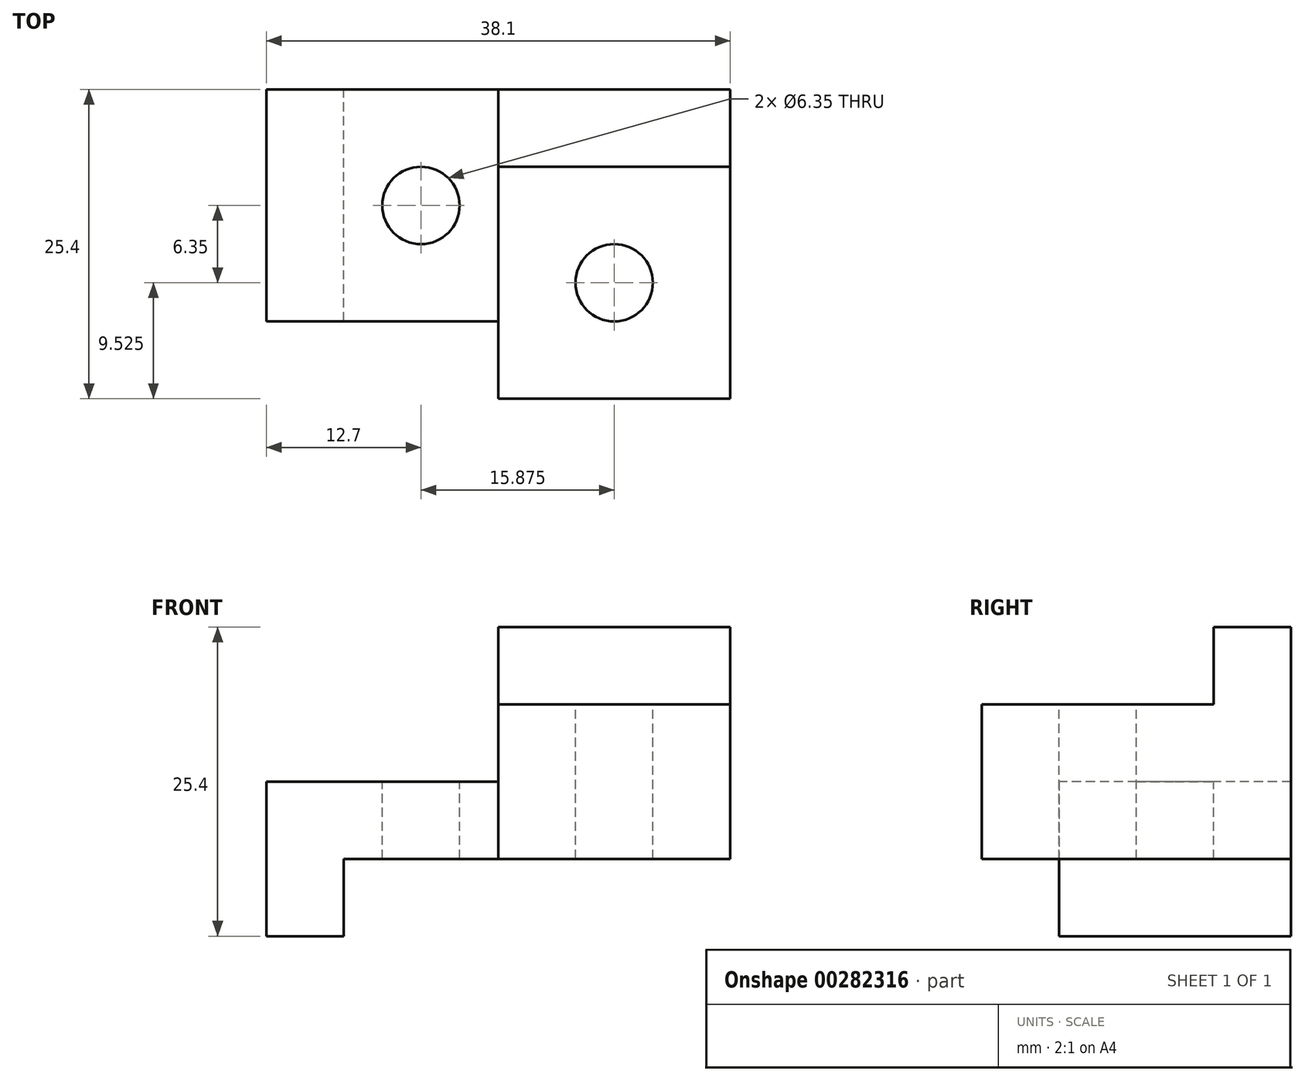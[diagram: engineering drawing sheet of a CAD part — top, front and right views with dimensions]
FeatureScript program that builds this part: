
annotation { "Feature Type Name" : "Feature", "Feature Type Description" : "" }
export const myFeature = defineFeature(function(context is Context, id is Id, definition is map)
    precondition{}
    {
        {
            var Q0;
            Q0=qCreatedBy(makeId("Top.planeOp"),FACE);
            var sketch = newSketch(context, id + "F0", { "sketchPlane" : qUnion([Q0])});
            skLineSegment(sketch, "E0", {"start": v(0, 0) * mm, "end": v(0, 6.35) * mm});
            skLineSegment(sketch, "E1", {"start": v(0, 6.35) * mm, "end": v(-19.05, 6.35) * mm});
            skLineSegment(sketch, "E2", {"start": v(-19.05, 6.35) * mm, "end": v(-19.05, 25.4) * mm});
            skLineSegment(sketch, "E3", {"start": v(-19.05, 25.4) * mm, "end": v(0, 25.4) * mm});
            skLineSegment(sketch, "E4", {"start": v(0, 25.4) * mm, "end": v(19.05, 25.4) * mm});
            skLineSegment(sketch, "E5", {"start": v(19.05, 0) * mm, "end": v(0, 0) * mm});
            skLineSegment(sketch, "E6", {"start": v(19.05, 25.4) * mm, "end": v(19.05, 0) * mm});
            skSolve(sketch);
        }
        {
            var Q0;
            Q0 = qSketchRegion(id + "F0", true);
            extrude(context, id + "F1", {"entities" : qUnion([Q0]), "depth" : 6.35 * mm});
        }
        {
            var Q0;
            Q0=makeQuery(id+"F1.opExtrude","CAP_FACE",FACE,{"disambiguationData":[OSD([sQuery(id+"F0.wireOp",EDGE,"E0"),sQuery(id+"F0.wireOp",EDGE,"E1"),sQuery(id+"F0.wireOp",EDGE,"E2"),sQuery(id+"F0.wireOp",EDGE,"E3"),sQuery(id+"F0.wireOp",EDGE,"E4"),sQuery(id+"F0.wireOp",EDGE,"E5"),sQuery(id+"F0.wireOp",EDGE,"E6")])],"isStart":true});
            var sketch = newSketch(context, id + "F2", { "sketchPlane" : qUnion([Q0])});
            skLineSegment(sketch, "E7", {"start": v(-19.05, -6.35) * mm, "end": v(-12.7, -6.35) * mm});
            skLineSegment(sketch, "E8", {"start": v(-12.7, -6.35) * mm, "end": v(-12.7, -25.4) * mm});
            skLineSegment(sketch, "E9", {"start": v(-12.7, -25.4) * mm, "end": v(-19.05, -25.4) * mm});
            skLineSegment(sketch, "E10", {"start": v(-19.05, -25.4) * mm, "end": v(-19.05, -6.35) * mm});
            skSolve(sketch);
        }
        {
            var Q0;
            Q0 = qSketchRegion(id + "F2", true);
            extrude(context, id + "F3", {"entities" : qUnion([Q0]), "operationType" : NewBodyOperationType.ADD, "depth" : 6.35 * mm});
        }
        {
            var Q0;
            Q0=makeQuery(id+"F1.opExtrude","CAP_FACE",FACE,{"disambiguationData":[OSD([sQuery(id+"F0.wireOp",EDGE,"E0"),sQuery(id+"F0.wireOp",EDGE,"E1"),sQuery(id+"F0.wireOp",EDGE,"E2"),sQuery(id+"F0.wireOp",EDGE,"E3"),sQuery(id+"F0.wireOp",EDGE,"E4"),sQuery(id+"F0.wireOp",EDGE,"E5"),sQuery(id+"F0.wireOp",EDGE,"E6")])],"isStart":false});
            var sketch = newSketch(context, id + "F4", { "sketchPlane" : qUnion([Q0])});
            skLineSegment(sketch, "E11", {"start": v(0, 25.4) * mm, "end": v(0, 0) * mm});
            skLineSegment(sketch, "E12", {"start": v(0, 0) * mm, "end": v(19.05, 0) * mm});
            skLineSegment(sketch, "E13", {"start": v(19.05, 0) * mm, "end": v(19.05, 25.4) * mm});
            skLineSegment(sketch, "E14", {"start": v(19.05, 25.4) * mm, "end": v(0, 25.4) * mm});
            skSolve(sketch);
        }
        {
            var Q0;
            Q0 = qSketchRegion(id + "F4", true);
            extrude(context, id + "F5", {"entities" : qUnion([Q0]), "operationType" : NewBodyOperationType.ADD, "depth" : 6.35 * mm});
        }
        {
            var Q0;
            Q0=makeQuery(id+"F5.opExtrude","CAP_FACE",FACE,{"disambiguationData":[OSD([sQuery(id+"F4.wireOp",EDGE,"E11"),sQuery(id+"F4.wireOp",EDGE,"E12"),sQuery(id+"F4.wireOp",EDGE,"E13"),sQuery(id+"F4.wireOp",EDGE,"E14")])],"isStart":false});
            var sketch = newSketch(context, id + "F6", { "sketchPlane" : qUnion([Q0])});
            skLineSegment(sketch, "E15", {"start": v(0, 25.4) * mm, "end": v(0, 19.05) * mm});
            skLineSegment(sketch, "E16", {"start": v(0, 25.4) * mm, "end": v(19.05, 25.4) * mm});
            skLineSegment(sketch, "E17", {"start": v(19.05, 25.4) * mm, "end": v(19.05, 19.05) * mm});
            skLineSegment(sketch, "E18", {"start": v(19.05, 19.05) * mm, "end": v(0, 19.05) * mm});
            skSolve(sketch);
        }
        {
            var Q0;
            Q0 = qSketchRegion(id + "F6", true);
            extrude(context, id + "F7", {"entities" : qUnion([Q0]), "operationType" : NewBodyOperationType.ADD, "depth" : 6.35 * mm});
        }
        {
            var Q0;
            Q0=makeQuery(id+"F5.opExtrude","CAP_FACE",FACE,{"disambiguationData":[OSD([sQuery(id+"F4.wireOp",EDGE,"E11"),sQuery(id+"F4.wireOp",EDGE,"E12"),sQuery(id+"F4.wireOp",EDGE,"E13"),sQuery(id+"F4.wireOp",EDGE,"E14")])],"isStart":false});
            var sketch = newSketch(context, id + "F8", { "sketchPlane" : qUnion([Q0])});
            skCircle(sketch, "E19", {"center": v(9.52, 9.53) * mm, "radius": 3.18 * mm});
            skSolve(sketch);
        }
        {
            var Q0;
            Q0=makeQuery(id+"F8.imprint","IMPRINT",FACE,{"disambiguationData":[TD([[makeQuery(id+"F8.imprint","IMPRINT",EDGE,{"derivedFrom":sQuery(id+"F8.wireOp",EDGE,"E19")}),1.0]])]});
            extrude(context, id + "F9", {"entities" : qUnion([Q0]), "operationType" : NewBodyOperationType.REMOVE, "oppositeDirection" : true, "depth" : 12.7 * mm});
        }
        {
            var Q0;
            Q0=makeQuery(id+"F1.opExtrude","CAP_FACE",FACE,{"disambiguationData":[OSD([sQuery(id+"F0.wireOp",EDGE,"E0"),sQuery(id+"F0.wireOp",EDGE,"E1"),sQuery(id+"F0.wireOp",EDGE,"E2"),sQuery(id+"F0.wireOp",EDGE,"E3"),sQuery(id+"F0.wireOp",EDGE,"E4"),sQuery(id+"F0.wireOp",EDGE,"E5"),sQuery(id+"F0.wireOp",EDGE,"E6")])],"isStart":false});
            var sketch = newSketch(context, id + "F10", { "sketchPlane" : qUnion([Q0])});
            skCircle(sketch, "E20", {"center": v(-6.35, 15.88) * mm, "radius": 3.18 * mm});
            skSolve(sketch);
        }
        {
            var Q0;
            Q0 = qSketchRegion(id + "F10", true);
            extrude(context, id + "F11", {"entities" : qUnion([Q0]), "operationType" : NewBodyOperationType.REMOVE, "oppositeDirection" : true, "depth" : 6.35 * mm});
        }
    });
